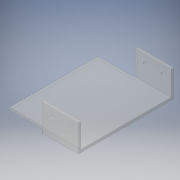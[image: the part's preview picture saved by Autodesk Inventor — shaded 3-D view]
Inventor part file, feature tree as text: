
AUTODESK INVENTOR PART (.ipt)
format: ipt  version: 2016 (Build 200138000, 138)  size: 129,536 bytes
history: native  units: in
note: dims shown in document units (in); Inventor stores cm internally (conversion verified against a paired STEP export)
features: sketch x5, extrude x4, hole x1
ambient origin geometry x8: Origin, YZ Plane, XZ Plane, XY Plane, X Axis, Y Axis, Z Axis, Center Point
bodies: Solid1 (feature_tree)
feature tree (10):
  extrude  "Extrusion1"  Depth=5.3in
  extrude  "Extrusion2"  Depth=5.0in
  extrude  "Extrusion3"  Depth=2.0in
  extrude  "Extrusion4"  Depth=0.2in TaperAngle=0.0deg
  hole  "Hole1"  [1 undecoded]
  sketch  "Sketch1"  dims[d0=4.0in d1=5.3in]
  sketch  "Sketch3"  dims[d2=1.5in d3=0.0in d4=5.0in]
  sketch  "Sketch4"  dims[d5=1.35in d6=0.0in d7=2.0in]
  sketch  "Sketch5"  dims[d8=0.2in d9=0.0in d10=0.2in d11=0.0in]
  sketch  "Sketch6"  dims[d12=0.5in d13=0.5in d14=0.5in d15=0.1457in d16=0.75in d17=0.375in d18=0.25in d19=0.5635in d20=1.0in d21=0.8108in]
note: 1 required parameter value undecoded (feature->parameter linkage not recoverable at this tier; creation-order binding heuristic only, values carry confidence <= 0.55)
